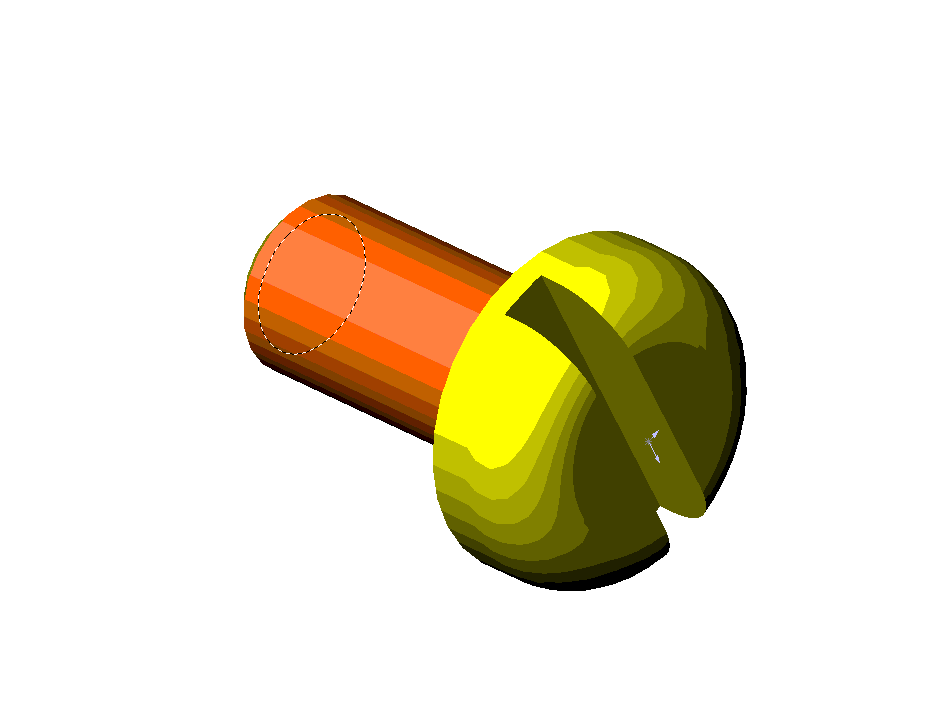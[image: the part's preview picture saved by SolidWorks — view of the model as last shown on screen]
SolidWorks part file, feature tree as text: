
SOLIDWORKS PART (.sldprt)
format: sldprt  version: not decoded by parser v0  size: 115,200 bytes
history: native  units: mm
features: plane x3, sketch x3, extrude x2, material x1, fillet x1, thread x1, chamfer x1, cut_extrude x1 (+10 scaffold rows collapsed)
feature tree (23):
  scaffold x10  (default folders/planes/origin — collapsed)
  material  "Matériau <non spécifié>"
  plane  "Plan1"
  plane  "Plan2"
  plane  "Plan3"
  sketch  "Esquisse1"  dims[D1=3.8mm]
  extrude  "Base-Extrusion"  Depth=1.3mm
  fillet  "Congé1"  Radius=0.8mm
  sketch  "Esquisse2"  dims[D1=2.0mm]
  extrude  "Boss.-Extru.1"  [1 undecoded]
  thread  "Représentation de filetage1"  [2 undecoded]
  chamfer  "Chanfrein1"  Distance=0.2mm Angle=45deg
  sketch  "Esquisse3"  dims[D1=0.6mm D2=1.0mm]
  cut_extrude  "Enlèv. mat.-Extru.1"  [1 undecoded]
decode coverage: 6 of 9 modeling features carry decoded parameters
note: 4 parameter values undecoded
summary: no parameter record found for 3 features
note: suppression state not decoded; provenance and decode notes live in map.json
